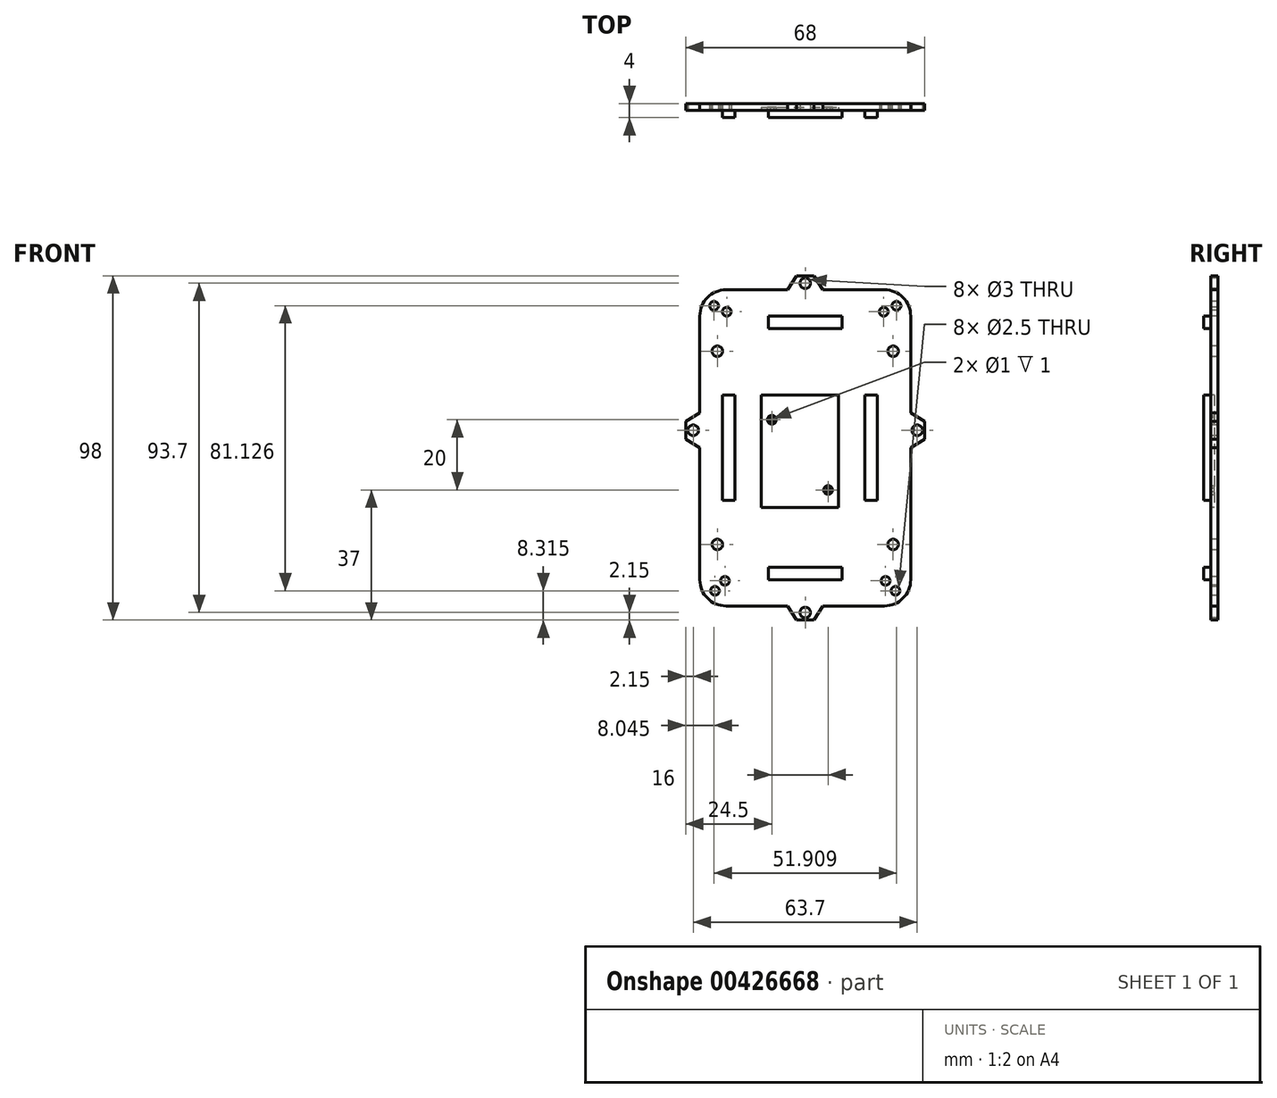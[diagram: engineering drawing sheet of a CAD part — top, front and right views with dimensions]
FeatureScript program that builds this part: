
annotation { "Feature Type Name" : "Feature", "Feature Type Description" : "" }
export const myFeature = defineFeature(function(context is Context, id is Id, definition is map)
    precondition{}
    {
        {
            var Q0;
            Q0=qCreatedBy(makeId("Front.planeOp"),FACE);
            var sketch = newSketch(context, id + "F0", { "sketchPlane" : qUnion([Q0])});
            skLineSegment(sketch, "E0.bottom", {"start": v(0, 0) * mm, "end": v(60, 0) * mm});
            skLineSegment(sketch, "E0.top", {"start": v(0, 90) * mm, "end": v(60, 90) * mm});
            skLineSegment(sketch, "E0.left", {"start": v(0, 0) * mm, "end": v(0, 90) * mm});
            skLineSegment(sketch, "E0.right", {"start": v(60, 0) * mm, "end": v(60, 90) * mm});
            skSolve(sketch);
        }
        {
            var Q0;
            Q0=makeQuery(id+"F0.imprint","IMPRINT",FACE,{"disambiguationData":[TD([[makeQuery(id+"F0.imprint","IMPRINT",EDGE,{"derivedFrom":sQuery(id+"F0.wireOp",EDGE,"E0.bottom")}),1.0]])]});
            extrude(context, id + "F1", {"entities" : qUnion([Q0]), "depth" : 2 * mm, "offsetDistance" : 25 * mm});
        }
        {
            var Q0;
            Q0=makeQuery(id+"F1.opExtrude","CAP_FACE",FACE,{"disambiguationData":[OSD([sQuery(id+"F0.wireOp",EDGE,"E0.bottom"),sQuery(id+"F0.wireOp",EDGE,"E0.top"),sQuery(id+"F0.wireOp",EDGE,"E0.left"),sQuery(id+"F0.wireOp",EDGE,"E0.right")])],"isStart":false});
            var sketch = newSketch(context, id + "F2", { "sketchPlane" : qUnion([Q0])});
            skLineSegment(sketch, "E1.bottom", {"start": v(17.5, 60) * mm, "end": v(39.5, 60) * mm});
            skLineSegment(sketch, "E1.top", {"start": v(17.5, 28) * mm, "end": v(39.5, 28) * mm});
            skLineSegment(sketch, "E1.left", {"start": v(17.5, 60) * mm, "end": v(17.5, 28) * mm});
            skLineSegment(sketch, "E1.right", {"start": v(39.5, 60) * mm, "end": v(39.5, 28) * mm});
            skSolve(sketch);
        }
        {
            var Q0;
            Q0 = qSketchRegion(id + "F2", true);
            extrude(context, id + "F3", {"entities" : qUnion([Q0]), "operationType" : NewBodyOperationType.REMOVE, "oppositeDirection" : true, "depth" : 1 * mm});
        }
        {
            var Q0;
            Q0=makeQuery(id+"F3.boolean.opBoolean","COPY",FACE,{"derivedFrom":makeQuery(id+"F3.opExtrude","CAP_FACE",FACE,{"disambiguationData":[OSD([sQuery(id+"F2.wireOp",EDGE,"E1.bottom"),sQuery(id+"F2.wireOp",EDGE,"E1.top"),sQuery(id+"F2.wireOp",EDGE,"E1.left"),sQuery(id+"F2.wireOp",EDGE,"E1.right")])],"isStart":false})});
            var sketch = newSketch(context, id + "F4", { "sketchPlane" : qUnion([Q0])});
            skCircle(sketch, "E2", {"center": v(20.5, 53) * mm, "radius": 1.25 * mm});
            skCircle(sketch, "E3", {"center": v(36.5, 33) * mm, "radius": 1.25 * mm});
            skSolve(sketch);
        }
        {
            var Q0;
            Q0 = qSketchRegion(id + "F4", true);
            extrude(context, id + "F5", {"entities" : qUnion([Q0]), "operationType" : NewBodyOperationType.ADD, "depth" : 1 * mm});
        }
        {
            var Q0;
            Q0=makeQuery(id+"F5.opExtrude","CAP_FACE",FACE,{"disambiguationData":[OSD([sQuery(id+"F4.wireOp",EDGE,"E2")])],"isStart":false});
            var sketch = newSketch(context, id + "F6", { "sketchPlane" : qUnion([Q0])});
            skCircle(sketch, "E4", {"center": v(20.5, 53) * mm, "radius": 0.5 * mm});
            skCircle(sketch, "E5", {"center": v(36.5, 33) * mm, "radius": 0.5 * mm});
            skSolve(sketch);
        }
        {
            var Q0;
            Q0=makeQuery(id+"F6.imprint","IMPRINT",FACE,{"disambiguationData":[TD([[makeQuery(id+"F6.imprint","IMPRINT",EDGE,{"derivedFrom":sQuery(id+"F6.wireOp",EDGE,"E4")}),1.0]])]});
            var Q1;
            Q1=makeQuery(id+"F6.imprint","IMPRINT",FACE,{"disambiguationData":[TD([[makeQuery(id+"F6.imprint","IMPRINT",EDGE,{"derivedFrom":sQuery(id+"F6.wireOp",EDGE,"E5")}),1.0]])]});
            extrude(context, id + "F7", {"entities" : qUnion([Q0, Q1]), "operationType" : NewBodyOperationType.REMOVE, "oppositeDirection" : true, "depth" : 1 * mm});
        }
        {
            var Q0;
            Q0=makeQuery(id+"F1.opExtrude","SWEPT_EDGE",EDGE,{"disambiguationData":[OSD([sQuery(id+"F0.wireOp",EDGE,"E0.top"),sQuery(id+"F0.wireOp",EDGE,"E0.right")])]});
            fillet(context, id + "F8", {"entities" : qUnion([Q0]), "radius" : 7.5 * mm, "tangentPropagation" : true, "allowEdgeOverflow" : false});
        }
        {
            var Q0;
            Q0=makeQuery(id+"F1.opExtrude","SWEPT_EDGE",EDGE,{"disambiguationData":[OSD([sQuery(id+"F0.wireOp",EDGE,"E0.top"),sQuery(id+"F0.wireOp",EDGE,"E0.left")])]});
            var Q1;
            Q1=makeQuery(id+"F1.opExtrude","SWEPT_EDGE",EDGE,{"disambiguationData":[OSD([sQuery(id+"F0.wireOp",EDGE,"E0.bottom"),sQuery(id+"F0.wireOp",EDGE,"E0.left")])]});
            var Q2;
            Q2=makeQuery(id+"F1.opExtrude","SWEPT_EDGE",EDGE,{"disambiguationData":[OSD([sQuery(id+"F0.wireOp",EDGE,"E0.bottom"),sQuery(id+"F0.wireOp",EDGE,"E0.right")])]});
            fillet(context, id + "F9", {"entities" : qUnion([Q0, Q1, Q2]), "radius" : 7.5 * mm, "tangentPropagation" : true, "allowEdgeOverflow" : false});
        }
        {
            var Q0;
            Q0=makeQuery(id+"F1.opExtrude","CAP_FACE",FACE,{"disambiguationData":[OSD([sQuery(id+"F0.wireOp",EDGE,"E0.bottom"),sQuery(id+"F0.wireOp",EDGE,"E0.top"),sQuery(id+"F0.wireOp",EDGE,"E0.left"),sQuery(id+"F0.wireOp",EDGE,"E0.right")])],"isStart":false});
            var sketch = newSketch(context, id + "F10", { "sketchPlane" : qUnion([Q0])});
            skLineSegment(sketch, "E6", {"start": v(25, 90) * mm, "end": v(27.5, 94) * mm});
            skLineSegment(sketch, "E7", {"start": v(27.5, 94) * mm, "end": v(32.5, 94) * mm});
            skLineSegment(sketch, "E8", {"start": v(32.5, 94) * mm, "end": v(35, 90) * mm});
            skLineSegment(sketch, "E9", {"start": v(60, 55) * mm, "end": v(64, 52.5) * mm});
            skLineSegment(sketch, "E10", {"start": v(64, 52.5) * mm, "end": v(64, 47.5) * mm});
            skLineSegment(sketch, "E11", {"start": v(64, 47.5) * mm, "end": v(60, 45) * mm});
            skLineSegment(sketch, "E12", {"start": v(35, 0) * mm, "end": v(32.5, -4) * mm});
            skLineSegment(sketch, "E13", {"start": v(32.5, -4) * mm, "end": v(27.5, -4) * mm});
            skLineSegment(sketch, "E14", {"start": v(27.5, -4) * mm, "end": v(25, 0) * mm});
            skLineSegment(sketch, "E15", {"start": v(0, 45) * mm, "end": v(-4, 47.5) * mm});
            skLineSegment(sketch, "E16", {"start": v(-4, 47.5) * mm, "end": v(-4, 52.5) * mm});
            skLineSegment(sketch, "E17", {"start": v(-4, 52.5) * mm, "end": v(0, 55) * mm});
            skSolve(sketch);
        }
        {
            var Q0;
            Q0 = qSketchRegion(id + "F10", true);
            var Q1;
            {var subQ0=sQuery(id+"F10.wireOp",EDGE,"E15");Q1=makeQuery(id+"F10.imprint","IMPRINT",FACE,{"disambiguationData":[TD([[makeQuery(id+"F10.imprint","IMPRINT",EDGE,{"derivedFrom":subQ0}),-1.0]])]});}
            var Q2;
            {var subQ0=sQuery(id+"F10.wireOp",EDGE,"E9");Q2=makeQuery(id+"F10.imprint","IMPRINT",FACE,{"disambiguationData":[TD([[makeQuery(id+"F10.imprint","IMPRINT",EDGE,{"derivedFrom":subQ0}),-1.0]])]});}
            var Q3;
            {var subQ0=sQuery(id+"F10.wireOp",EDGE,"E6");Q3=makeQuery(id+"F10.imprint","IMPRINT",FACE,{"disambiguationData":[TD([[makeQuery(id+"F10.imprint","IMPRINT",EDGE,{"derivedFrom":subQ0}),-1.0]])]});}
            var Q4;
            {var subQ0=sQuery(id+"F10.wireOp",EDGE,"E12");Q4=makeQuery(id+"F10.imprint","IMPRINT",FACE,{"disambiguationData":[TD([[makeQuery(id+"F10.imprint","IMPRINT",EDGE,{"derivedFrom":subQ0}),-1.0]])]});}
            extrude(context, id + "F11", {"entities" : qUnion([Q0, Q1, Q2, Q3, Q4]), "operationType" : NewBodyOperationType.ADD, "oppositeDirection" : true, "depth" : 2 * mm});
        }
        {
            var Q0;
            {var subQ0=sQuery(id+"F0.wireOp",EDGE,"E0.left");var subQ1=sQuery(id+"F0.wireOp",EDGE,"E0.bottom");var subQ2=sQuery(id+"F0.wireOp",EDGE,"E0.right");var subQ3=sQuery(id+"F0.wireOp",EDGE,"E0.top");Q0=makeQuery(id+"F11.boolean.opBoolean","MERGE",FACE,{"derivedFrom":[makeQuery(id+"F1.opExtrude","CAP_FACE",FACE,{"disambiguationData":[OSD([subQ1,subQ3,subQ0,subQ2])],"isStart":false}),makeQuery(id+"F11.opExtrude","CAP_FACE",FACE,{"disambiguationData":[OSD([subQ3,sQuery(id+"F10.wireOp",EDGE,"E6"),sQuery(id+"F10.wireOp",EDGE,"E7"),sQuery(id+"F10.wireOp",EDGE,"E8")])],"isStart":true}),makeQuery(id+"F11.opExtrude","CAP_FACE",FACE,{"disambiguationData":[OSD([subQ2,sQuery(id+"F10.wireOp",EDGE,"E9"),sQuery(id+"F10.wireOp",EDGE,"E10"),sQuery(id+"F10.wireOp",EDGE,"E11")])],"isStart":true}),makeQuery(id+"F11.opExtrude","CAP_FACE",FACE,{"disambiguationData":[OSD([subQ1,sQuery(id+"F10.wireOp",EDGE,"E12"),sQuery(id+"F10.wireOp",EDGE,"E13"),sQuery(id+"F10.wireOp",EDGE,"E14")])],"isStart":true}),makeQuery(id+"F11.opExtrude","CAP_FACE",FACE,{"disambiguationData":[OSD([subQ0,sQuery(id+"F10.wireOp",EDGE,"E15"),sQuery(id+"F10.wireOp",EDGE,"E16"),sQuery(id+"F10.wireOp",EDGE,"E17")])],"isStart":true})]});}
            var sketch = newSketch(context, id + "F12", { "sketchPlane" : qUnion([Q0])});
            skPoint(sketch, "E18.centerSnap0", {"position": v(-2, 46.25) * mm});
            skPoint(sketch, "E19.centerSnap0", {"position": v(64, 50) * mm});
            skPoint(sketch, "E20.centerSnap0", {"position": v(30, 94) * mm});
            skPoint(sketch, "E20.centerSnap1", {"position": v(26.25, 92) * mm});
            skCircle(sketch, "E21", {"center": v(30, 91.85) * mm, "radius": 1.5 * mm});
            skCircle(sketch, "E22", {"center": v(61.85, 50) * mm, "radius": 1.5 * mm});
            skCircle(sketch, "E23", {"center": v(30, -1.85) * mm, "radius": 1.5 * mm});
            skCircle(sketch, "E24", {"center": v(-1.85, 50) * mm, "radius": 1.5 * mm});
            skSolve(sketch);
        }
        {
            var Q0;
            Q0 = qSketchRegion(id + "F12", true);
            extrude(context, id + "F13", {"entities" : qUnion([Q0]), "operationType" : NewBodyOperationType.REMOVE, "oppositeDirection" : true, "depth" : 3 * mm});
        }
        {
            var Q0;
            {var subQ0=sQuery(id+"F0.wireOp",EDGE,"E0.left");var subQ1=sQuery(id+"F0.wireOp",EDGE,"E0.bottom");var subQ2=sQuery(id+"F0.wireOp",EDGE,"E0.right");var subQ3=sQuery(id+"F0.wireOp",EDGE,"E0.top");Q0=makeQuery(id+"F11.boolean.opBoolean","MERGE",FACE,{"derivedFrom":[makeQuery(id+"F1.opExtrude","CAP_FACE",FACE,{"disambiguationData":[OSD([subQ1,subQ3,subQ0,subQ2])],"isStart":false}),makeQuery(id+"F11.opExtrude","CAP_FACE",FACE,{"disambiguationData":[OSD([subQ3,sQuery(id+"F10.wireOp",EDGE,"E6"),sQuery(id+"F10.wireOp",EDGE,"E7"),sQuery(id+"F10.wireOp",EDGE,"E8")])],"isStart":true}),makeQuery(id+"F11.opExtrude","CAP_FACE",FACE,{"disambiguationData":[OSD([subQ2,sQuery(id+"F10.wireOp",EDGE,"E9"),sQuery(id+"F10.wireOp",EDGE,"E10"),sQuery(id+"F10.wireOp",EDGE,"E11")])],"isStart":true}),makeQuery(id+"F11.opExtrude","CAP_FACE",FACE,{"disambiguationData":[OSD([subQ1,sQuery(id+"F10.wireOp",EDGE,"E12"),sQuery(id+"F10.wireOp",EDGE,"E13"),sQuery(id+"F10.wireOp",EDGE,"E14")])],"isStart":true}),makeQuery(id+"F11.opExtrude","CAP_FACE",FACE,{"disambiguationData":[OSD([subQ0,sQuery(id+"F10.wireOp",EDGE,"E15"),sQuery(id+"F10.wireOp",EDGE,"E16"),sQuery(id+"F10.wireOp",EDGE,"E17")])],"isStart":true})]});}
            var sketch = newSketch(context, id + "F14", { "sketchPlane" : qUnion([Q0])});
            skLineSegment(sketch, "E25.bottom", {"start": v(10, 30) * mm, "end": v(6.5, 30) * mm});
            skLineSegment(sketch, "E25.top", {"start": v(10, 60) * mm, "end": v(6.5, 60) * mm});
            skLineSegment(sketch, "E25.left", {"start": v(10, 30) * mm, "end": v(10, 60) * mm});
            skLineSegment(sketch, "E25.right", {"start": v(6.5, 30) * mm, "end": v(6.5, 60) * mm});
            skLineSegment(sketch, "E26.bottom", {"start": v(47, 30) * mm, "end": v(50.5, 30) * mm});
            skLineSegment(sketch, "E26.top", {"start": v(47, 60) * mm, "end": v(50.5, 60) * mm});
            skLineSegment(sketch, "E26.left", {"start": v(47, 30) * mm, "end": v(47, 60) * mm});
            skLineSegment(sketch, "E26.right", {"start": v(50.5, 30) * mm, "end": v(50.5, 60) * mm});
            skSolve(sketch);
        }
        {
            var Q0;
            Q0 = qSketchRegion(id + "F14", true);
            extrude(context, id + "F15", {"entities" : qUnion([Q0]), "operationType" : NewBodyOperationType.ADD, "depth" : 2 * mm, "offsetDistance" : 25 * mm});
        }
        {
            var Q0;
            {var subQ0=sQuery(id+"F0.wireOp",EDGE,"E0.left");var subQ1=sQuery(id+"F0.wireOp",EDGE,"E0.bottom");var subQ2=sQuery(id+"F0.wireOp",EDGE,"E0.right");var subQ3=sQuery(id+"F0.wireOp",EDGE,"E0.top");Q0=makeQuery(id+"F11.boolean.opBoolean","MERGE",FACE,{"derivedFrom":[makeQuery(id+"F1.opExtrude","CAP_FACE",FACE,{"disambiguationData":[OSD([subQ1,subQ3,subQ0,subQ2])],"isStart":false}),makeQuery(id+"F11.opExtrude","CAP_FACE",FACE,{"disambiguationData":[OSD([subQ3,sQuery(id+"F10.wireOp",EDGE,"E6"),sQuery(id+"F10.wireOp",EDGE,"E7"),sQuery(id+"F10.wireOp",EDGE,"E8")])],"isStart":true}),makeQuery(id+"F11.opExtrude","CAP_FACE",FACE,{"disambiguationData":[OSD([subQ2,sQuery(id+"F10.wireOp",EDGE,"E9"),sQuery(id+"F10.wireOp",EDGE,"E10"),sQuery(id+"F10.wireOp",EDGE,"E11")])],"isStart":true}),makeQuery(id+"F11.opExtrude","CAP_FACE",FACE,{"disambiguationData":[OSD([subQ1,sQuery(id+"F10.wireOp",EDGE,"E12"),sQuery(id+"F10.wireOp",EDGE,"E13"),sQuery(id+"F10.wireOp",EDGE,"E14")])],"isStart":true}),makeQuery(id+"F11.opExtrude","CAP_FACE",FACE,{"disambiguationData":[OSD([subQ0,sQuery(id+"F10.wireOp",EDGE,"E15"),sQuery(id+"F10.wireOp",EDGE,"E16"),sQuery(id+"F10.wireOp",EDGE,"E17")])],"isStart":true})]});}
            var sketch = newSketch(context, id + "F16", { "sketchPlane" : qUnion([Q0])});
            skLineSegment(sketch, "E27.bottom", {"start": v(40.5, 11) * mm, "end": v(19.5, 11) * mm});
            skLineSegment(sketch, "E27.top", {"start": v(40.5, 7.5) * mm, "end": v(19.5, 7.5) * mm});
            skLineSegment(sketch, "E27.left", {"start": v(40.5, 11) * mm, "end": v(40.5, 7.5) * mm});
            skLineSegment(sketch, "E27.right", {"start": v(19.5, 11) * mm, "end": v(19.5, 7.5) * mm});
            skSolve(sketch);
        }
        {
            var Q0;
            Q0 = qSketchRegion(id + "F16", true);
            extrude(context, id + "F17", {"entities" : qUnion([Q0]), "operationType" : NewBodyOperationType.ADD, "depth" : 2 * mm, "offsetDistance" : 25 * mm});
        }
        {
            var Q0;
            {var subQ0=sQuery(id+"F0.wireOp",EDGE,"E0.left");var subQ1=sQuery(id+"F0.wireOp",EDGE,"E0.bottom");var subQ2=sQuery(id+"F0.wireOp",EDGE,"E0.right");var subQ3=sQuery(id+"F0.wireOp",EDGE,"E0.top");Q0=makeQuery(id+"F11.boolean.opBoolean","MERGE",FACE,{"derivedFrom":[makeQuery(id+"F1.opExtrude","CAP_FACE",FACE,{"disambiguationData":[OSD([subQ1,subQ3,subQ0,subQ2])],"isStart":false}),makeQuery(id+"F11.opExtrude","CAP_FACE",FACE,{"disambiguationData":[OSD([subQ3,sQuery(id+"F10.wireOp",EDGE,"E6"),sQuery(id+"F10.wireOp",EDGE,"E7"),sQuery(id+"F10.wireOp",EDGE,"E8")])],"isStart":true}),makeQuery(id+"F11.opExtrude","CAP_FACE",FACE,{"disambiguationData":[OSD([subQ2,sQuery(id+"F10.wireOp",EDGE,"E9"),sQuery(id+"F10.wireOp",EDGE,"E10"),sQuery(id+"F10.wireOp",EDGE,"E11")])],"isStart":true}),makeQuery(id+"F11.opExtrude","CAP_FACE",FACE,{"disambiguationData":[OSD([subQ1,sQuery(id+"F10.wireOp",EDGE,"E12"),sQuery(id+"F10.wireOp",EDGE,"E13"),sQuery(id+"F10.wireOp",EDGE,"E14")])],"isStart":true}),makeQuery(id+"F11.opExtrude","CAP_FACE",FACE,{"disambiguationData":[OSD([subQ0,sQuery(id+"F10.wireOp",EDGE,"E15"),sQuery(id+"F10.wireOp",EDGE,"E16"),sQuery(id+"F10.wireOp",EDGE,"E17")])],"isStart":true})]});}
            var sketch = newSketch(context, id + "F18", { "sketchPlane" : qUnion([Q0])});
            skLineSegment(sketch, "E28.bottom", {"start": v(40.5, 82.5) * mm, "end": v(19.5, 82.5) * mm});
            skLineSegment(sketch, "E28.top", {"start": v(40.5, 79) * mm, "end": v(19.5, 79) * mm});
            skLineSegment(sketch, "E28.left", {"start": v(40.5, 82.5) * mm, "end": v(40.5, 79) * mm});
            skLineSegment(sketch, "E28.right", {"start": v(19.5, 82.5) * mm, "end": v(19.5, 79) * mm});
            skSolve(sketch);
        }
        {
            var Q0;
            Q0 = qSketchRegion(id + "F18", true);
            extrude(context, id + "F19", {"entities" : qUnion([Q0]), "operationType" : NewBodyOperationType.ADD, "depth" : 2 * mm, "offsetDistance" : 25 * mm});
        }
        {
            var Q0;
            {var subQ0=sQuery(id+"F0.wireOp",EDGE,"E0.left");var subQ1=sQuery(id+"F0.wireOp",EDGE,"E0.bottom");var subQ2=sQuery(id+"F0.wireOp",EDGE,"E0.right");var subQ3=sQuery(id+"F0.wireOp",EDGE,"E0.top");Q0=makeQuery(id+"F11.boolean.opBoolean","MERGE",FACE,{"derivedFrom":[makeQuery(id+"F1.opExtrude","CAP_FACE",FACE,{"disambiguationData":[OSD([subQ1,subQ3,subQ0,subQ2])],"isStart":false}),makeQuery(id+"F11.opExtrude","CAP_FACE",FACE,{"disambiguationData":[OSD([subQ3,sQuery(id+"F10.wireOp",EDGE,"E6"),sQuery(id+"F10.wireOp",EDGE,"E7"),sQuery(id+"F10.wireOp",EDGE,"E8")])],"isStart":true}),makeQuery(id+"F11.opExtrude","CAP_FACE",FACE,{"disambiguationData":[OSD([subQ2,sQuery(id+"F10.wireOp",EDGE,"E9"),sQuery(id+"F10.wireOp",EDGE,"E10"),sQuery(id+"F10.wireOp",EDGE,"E11")])],"isStart":true}),makeQuery(id+"F11.opExtrude","CAP_FACE",FACE,{"disambiguationData":[OSD([subQ1,sQuery(id+"F10.wireOp",EDGE,"E12"),sQuery(id+"F10.wireOp",EDGE,"E13"),sQuery(id+"F10.wireOp",EDGE,"E14")])],"isStart":true}),makeQuery(id+"F11.opExtrude","CAP_FACE",FACE,{"disambiguationData":[OSD([subQ0,sQuery(id+"F10.wireOp",EDGE,"E15"),sQuery(id+"F10.wireOp",EDGE,"E16"),sQuery(id+"F10.wireOp",EDGE,"E17")])],"isStart":true})]});}
            var sketch = newSketch(context, id + "F20", { "sketchPlane" : qUnion([Q0])});
            skCircle(sketch, "E29", {"center": v(4.05, 85.44) * mm, "radius": 1.25 * mm});
            skCircle(sketch, "E30", {"center": v(55.95, 85.44) * mm, "radius": 1.25 * mm});
            skCircle(sketch, "E31", {"center": v(55.68, 4.31) * mm, "radius": 1.25 * mm});
            skCircle(sketch, "E32", {"center": v(4.32, 4.32) * mm, "radius": 1.25 * mm});
            skCircle(sketch, "E33", {"center": v(7.15, 7.15) * mm, "radius": 1.25 * mm});
            skCircle(sketch, "E34", {"center": v(52.86, 7.15) * mm, "radius": 1.25 * mm});
            skCircle(sketch, "E35", {"center": v(52.33, 83.75) * mm, "radius": 1.25 * mm});
            skCircle(sketch, "E36", {"center": v(7.67, 83.75) * mm, "radius": 1.25 * mm});
            skPoint(sketch, "E37.orphan", {"position": v(52.5, 82.5) * mm});
            skPoint(sketch, "E38.start.orphan", {"position": v(57.8, 87.8) * mm});
            skPoint(sketch, "E39.start.orphan", {"position": v(2.2, 87.8) * mm});
            skPoint(sketch, "E40.trimOffspring.end.orphan", {"position": v(7.5, 82.5) * mm});
            skPoint(sketch, "E41.orphan", {"position": v(2.2, 2.2) * mm});
            skPoint(sketch, "E42.end.orphan", {"position": v(7.5, 7.5) * mm});
            skPoint(sketch, "E43.orphan", {"position": v(52.5, 7.5) * mm});
            skPoint(sketch, "E44.start.orphan", {"position": v(57.8, 2.2) * mm});
            skSolve(sketch);
        }
        {
            var Q0;
            Q0 = qSketchRegion(id + "F20", true);
            extrude(context, id + "F21", {"entities" : qUnion([Q0]), "operationType" : NewBodyOperationType.REMOVE, "oppositeDirection" : true, "depth" : 25 * mm});
        }
        {
            var Q0;
            {var subQ0=sQuery(id+"F0.wireOp",EDGE,"E0.left");var subQ1=sQuery(id+"F0.wireOp",EDGE,"E0.bottom");var subQ2=sQuery(id+"F0.wireOp",EDGE,"E0.right");var subQ3=sQuery(id+"F0.wireOp",EDGE,"E0.top");Q0=makeQuery(id+"F11.boolean.opBoolean","MERGE",FACE,{"derivedFrom":[makeQuery(id+"F1.opExtrude","CAP_FACE",FACE,{"disambiguationData":[OSD([subQ1,subQ3,subQ0,subQ2])],"isStart":false}),makeQuery(id+"F11.opExtrude","CAP_FACE",FACE,{"disambiguationData":[OSD([subQ3,sQuery(id+"F10.wireOp",EDGE,"E6"),sQuery(id+"F10.wireOp",EDGE,"E7"),sQuery(id+"F10.wireOp",EDGE,"E8")])],"isStart":true}),makeQuery(id+"F11.opExtrude","CAP_FACE",FACE,{"disambiguationData":[OSD([subQ2,sQuery(id+"F10.wireOp",EDGE,"E9"),sQuery(id+"F10.wireOp",EDGE,"E10"),sQuery(id+"F10.wireOp",EDGE,"E11")])],"isStart":true}),makeQuery(id+"F11.opExtrude","CAP_FACE",FACE,{"disambiguationData":[OSD([subQ1,sQuery(id+"F10.wireOp",EDGE,"E12"),sQuery(id+"F10.wireOp",EDGE,"E13"),sQuery(id+"F10.wireOp",EDGE,"E14")])],"isStart":true}),makeQuery(id+"F11.opExtrude","CAP_FACE",FACE,{"disambiguationData":[OSD([subQ0,sQuery(id+"F10.wireOp",EDGE,"E15"),sQuery(id+"F10.wireOp",EDGE,"E16"),sQuery(id+"F10.wireOp",EDGE,"E17")])],"isStart":true})]});}
            var sketch = newSketch(context, id + "F22", { "sketchPlane" : qUnion([Q0])});
            skCircle(sketch, "E45", {"center": v(5, 72.5) * mm, "radius": 1.5 * mm});
            skCircle(sketch, "E46", {"center": v(5, 17.5) * mm, "radius": 1.5 * mm});
            skCircle(sketch, "E47", {"center": v(55, 72.5) * mm, "radius": 1.5 * mm});
            skCircle(sketch, "E48", {"center": v(55, 17.5) * mm, "radius": 1.5 * mm});
            skSolve(sketch);
        }
        {
            var Q0;
            Q0 = qSketchRegion(id + "F22", true);
            extrude(context, id + "F23", {"entities" : qUnion([Q0]), "operationType" : NewBodyOperationType.REMOVE, "oppositeDirection" : true, "depth" : 25 * mm, "offsetDistance" : 25 * mm});
        }
    });
